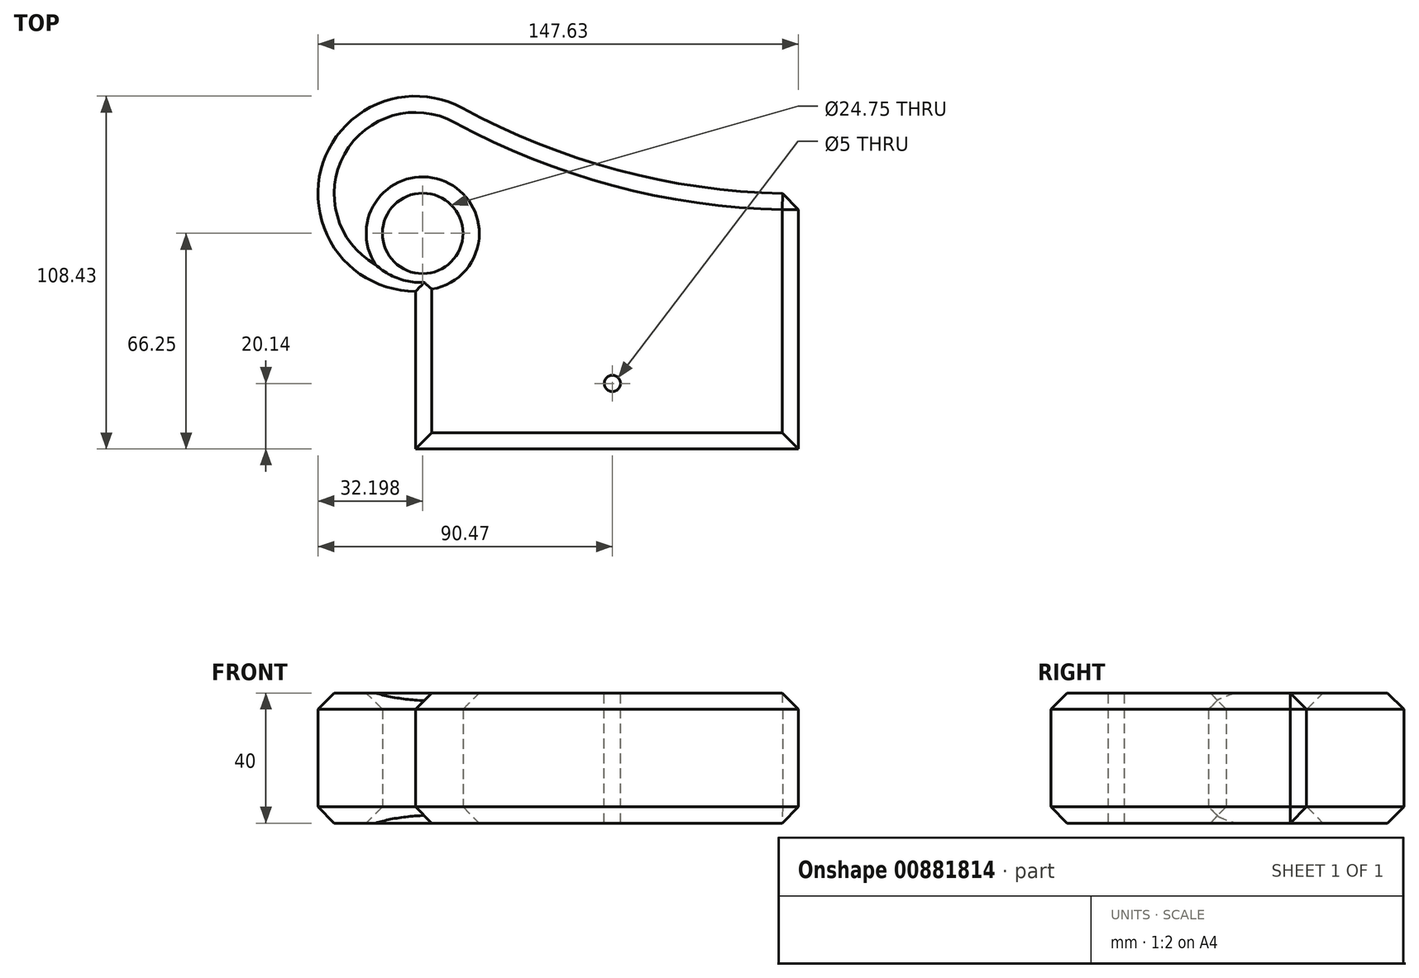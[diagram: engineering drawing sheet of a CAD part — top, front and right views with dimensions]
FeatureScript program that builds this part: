
annotation { "Feature Type Name" : "Feature", "Feature Type Description" : "" }
export const myFeature = defineFeature(function(context is Context, id is Id, definition is map)
    precondition{}
    {
        {
            var Q0;
            Q0=qCreatedBy(makeId("Top.planeOp"),FACE);
            var sketch = newSketch(context, id + "F0", { "sketchPlane" : qUnion([Q0])});
            skPoint(sketch, "E0.middle", {"position": v(0, 0) * mm});
            skLineSegment(sketch, "E1.bottom", {"start": v(-60.47, 35.99) * mm, "end": v(57.16, 35.99) * mm});
            skLineSegment(sketch, "E1.top", {"start": v(-60.47, -42.44) * mm, "end": v(57.16, -42.44) * mm});
            skLineSegment(sketch, "E1.left", {"start": v(-60.47, 35.99) * mm, "end": v(-60.47, -42.44) * mm});
            skLineSegment(sketch, "E1.right", {"start": v(57.16, 35.99) * mm, "end": v(57.16, -42.44) * mm});
            skCircle(sketch, "E2", {"center": v(-60.47, 35.99) * mm, "radius": 30 * mm});
            skArc(sketch, "E3", {"start": v(-46.1, 62.32) * mm, "mid": v(3.87, 42.68) * mm, "end": v(57.16, 35.99) * mm});
            skCircle(sketch, "E4", {"center": v(-58.27, 23.8) * mm, "radius": 12.38 * mm});
            skSolve(sketch);
        }
        {
            var Q0;
            Q0 = qSketchRegion(id + "F0", true);
            var Q1;
            Q1 = qSketchRegion(id + "F3", true);
            extrude(context, id + "F1", {"entities" : qUnion([Q0, Q1]), "depth" : 40 * mm, "offsetDistance" : 25 * mm});
        }
        {
            var Q0;
            Q0=makeQuery(id+"F1.opExtrude","CAP_FACE",FACE,{"disambiguationData":[OSD([sQuery(id+"F0.wireOp",EDGE,"E1.top"),sQuery(id+"F0.wireOp",EDGE,"E1.left"),sQuery(id+"F0.wireOp",EDGE,"E1.right"),sQuery(id+"F0.wireOp",EDGE,"E2"),sQuery(id+"F0.wireOp",EDGE,"E3")])],"isStart":false});
            var Q1;
            Q1=makeQuery(id+"F1.opExtrude","CAP_FACE",FACE,{"disambiguationData":[OSD([sQuery(id+"F0.wireOp",EDGE,"E1.top"),sQuery(id+"F0.wireOp",EDGE,"E1.left"),sQuery(id+"F0.wireOp",EDGE,"E1.right"),sQuery(id+"F0.wireOp",EDGE,"E2"),sQuery(id+"F0.wireOp",EDGE,"E3")])],"isStart":true});
            var Q2;
            Q2=makeQuery(id+"F1.opExtrude","SWEPT_EDGE",EDGE,{"disambiguationData":[OSD([sQuery(id+"F0.wireOp",EDGE,"E1.bottom"),sQuery(id+"F0.wireOp",EDGE,"E1.right"),sQuery(id+"F0.wireOp",EDGE,"E3")])]});
            var Q3;
            Q3=makeQuery(id+"F1.opExtrude","CAP_EDGE",EDGE,{"disambiguationData":[OSD([sQuery(id+"F0.wireOp",EDGE,"E1.top")])],"isStart":false});
            var Q4;
            Q4=makeQuery(id+"F1.opExtrude","CAP_EDGE",EDGE,{"disambiguationData":[OSD([sQuery(id+"F0.wireOp",EDGE,"E1.right")])],"isStart":false});
            chamfer(context, id + "F2", {"entities" : qUnion([Q0, Q1, Q2, Q3, Q4]), "width" : 5 * mm, "tangentPropagation" : true});
        }
        {
            var Q0;
            Q0=makeQuery(id+"F1.opExtrude","CAP_FACE",FACE,{"disambiguationData":[OSD([sQuery(id+"F0.wireOp",EDGE,"E1.top"),sQuery(id+"F0.wireOp",EDGE,"E1.left"),sQuery(id+"F0.wireOp",EDGE,"E1.right"),sQuery(id+"F0.wireOp",EDGE,"E2"),sQuery(id+"F0.wireOp",EDGE,"E3")])],"isStart":false});
            var sketch = newSketch(context, id + "F3", { "sketchPlane" : qUnion([Q0])});
            skCircle(sketch, "E5", {"center": v(-60.47, 35.99) * mm, "radius": 10.5 * mm});
            skPoint(sketch, "E6", {"position": v(-66.93, 52.37) * mm});
            skSolve(sketch);
        }
        {
            var Q0;
            Q0=makeQuery(id+"F3.imprint","IMPRINT",FACE,{"disambiguationData":[TD([[makeQuery(id+"F3.imprint","IMPRINT",EDGE,{"derivedFrom":sQuery(id+"F3.wireOp",EDGE,"E5")}),1.0]])]});
            extrude(context, id + "F4", {"entities" : qUnion([Q0]), "operationType" : NewBodyOperationType.REMOVE, "depth" : 40 * mm, "offsetDistance" : 25 * mm});
        }
        {
            var Q0;
            Q0=makeQuery(id+"F1.opExtrude","CAP_FACE",FACE,{"disambiguationData":[OSD([sQuery(id+"F0.wireOp",EDGE,"E1.top"),sQuery(id+"F0.wireOp",EDGE,"E1.left"),sQuery(id+"F0.wireOp",EDGE,"E1.right"),sQuery(id+"F0.wireOp",EDGE,"E2"),sQuery(id+"F0.wireOp",EDGE,"E3")])],"isStart":false});
            var sketch = newSketch(context, id + "F5", { "sketchPlane" : qUnion([Q0])});
            skPoint(sketch, "E7", {"position": v(-23.07, 29.98) * mm});
            skPoint(sketch, "E8", {"position": v(-2.98, 27.91) * mm});
            skPoint(sketch, "E9", {"position": v(22.42, 26.44) * mm});
            skPoint(sketch, "E10", {"position": v(44.87, 23.48) * mm});
            skPoint(sketch, "E11", {"position": v(48.41, 11.5) * mm});
            skPoint(sketch, "E12", {"position": v(48.41, 0) * mm});
            skPoint(sketch, "E13", {"position": v(52.16, -14.32) * mm});
            skPoint(sketch, "E14", {"position": v(45.46, -25.55) * mm});
            skPoint(sketch, "E15", {"position": v(28.33, -28.2) * mm});
            skPoint(sketch, "E16", {"position": v(0, -22.3) * mm});
            skPoint(sketch, "E17", {"position": v(-29.27, -21.41) * mm});
            skPoint(sketch, "E18", {"position": v(-36.95, -2.51) * mm});
            skPoint(sketch, "E19", {"position": v(-35.18, 17.58) * mm});
            skPoint(sketch, "E20", {"position": v(-29.27, 26.44) * mm});
            skSolve(sketch);
        }
        {
            var Q0;
            Q0=sQuery(id+"F5.wireOp",VERTEX,"E16");
            var Q1;
            Q1=makeQuery(id+"F1.opExtrude","SWEPT_BODY",BODY,{"disambiguationData":[OSD([sQuery(id+"F0.wireOp",EDGE,"E1.top"),sQuery(id+"F0.wireOp",EDGE,"E1.left"),sQuery(id+"F0.wireOp",EDGE,"E1.right"),sQuery(id+"F0.wireOp",EDGE,"E2"),sQuery(id+"F0.wireOp",EDGE,"E3")])]});
            hole(context, id + "F6", {"style" : HoleStyle.SIMPLE, "endStyle" : HoleEndStyle.THROUGH, "holeDiameter" : 5 * mm, "majorDiameter" : 5 * mm, "isTappedThrough" : true, "tappedDepth" : 12 * mm, "tapClearance" : 3, "locations" : qUnion([Q0]), "scope" : qUnion([Q1])});
        }
    });
